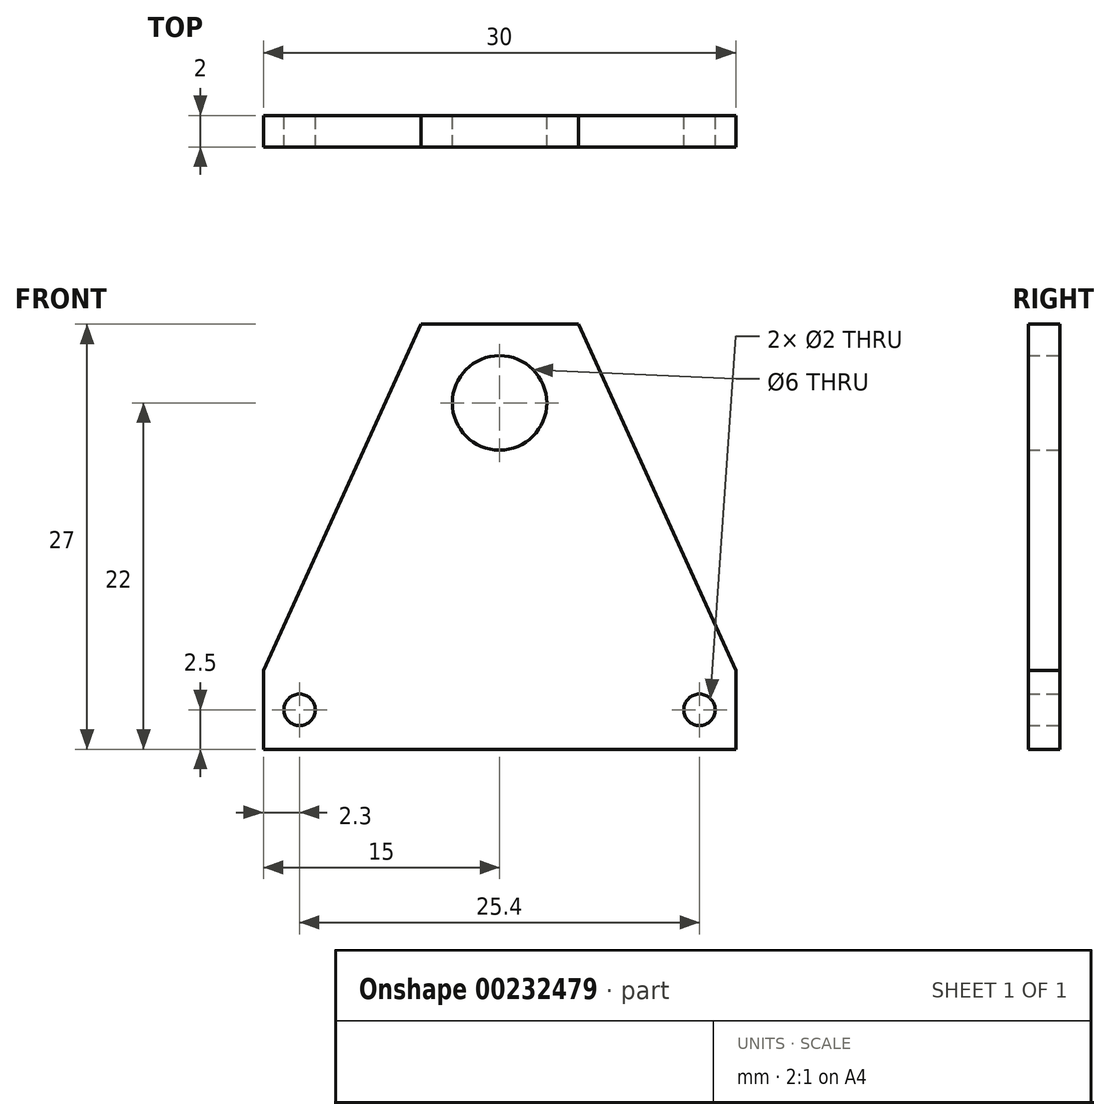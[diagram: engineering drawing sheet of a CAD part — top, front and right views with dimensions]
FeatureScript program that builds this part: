
annotation { "Feature Type Name" : "Feature", "Feature Type Description" : "" }
export const myFeature = defineFeature(function(context is Context, id is Id, definition is map)
    precondition{}
    {
        {
            var Q0;
            Q0=qCreatedBy(makeId("Front.planeOp"),FACE);
            var sketch = newSketch(context, id + "F0", { "sketchPlane" : qUnion([Q0])});
            skLineSegment(sketch, "E0", {"start": v(0, 0) * mm, "end": v(15, 0) * mm});
            skLineSegment(sketch, "E1", {"start": v(15, 0) * mm, "end": v(15, 5) * mm});
            skLineSegment(sketch, "E2", {"start": v(0, 27) * mm, "end": v(5, 27) * mm});
            skLineSegment(sketch, "E3", {"start": v(5, 27) * mm, "end": v(15, 5) * mm});
            skCircle(sketch, "E4", {"center": v(12.7, 2.5) * mm, "radius": 1 * mm});
            skCircle(sketch, "E5", {"center": v(0, 22) * mm, "radius": 3 * mm});
            skLineSegment(sketch, "E6.MirrorCS", {"start": v(0, 27) * mm, "end": v(-5, 27) * mm});
            skLineSegment(sketch, "E7.MirrorCS", {"start": v(-5, 27) * mm, "end": v(-15, 5) * mm});
            skLineSegment(sketch, "E8.MirrorCS", {"start": v(-15, 0) * mm, "end": v(-15, 5) * mm});
            skCircle(sketch, "E9.MirrorC", {"center": v(-12.7, 2.5) * mm, "radius": 1 * mm});
            skLineSegment(sketch, "E10.MirrorCS", {"start": v(0, 0) * mm, "end": v(-15, 0) * mm});
            skSolve(sketch);
        }
        {
            var Q0;
            Q0=makeQuery(id+"F0.imprint","IMPRINT",FACE,{"disambiguationData":[TD([[makeQuery(id+"F0.imprint","IMPRINT",EDGE,{"derivedFrom":sQuery(id+"F0.wireOp",EDGE,"E0")}),1.0]])]});
            extrude(context, id + "F1", {"entities" : qUnion([Q0]), "endBound" : BoundingType.SYMMETRIC, "depth" : 2 * mm});
        }
    });
